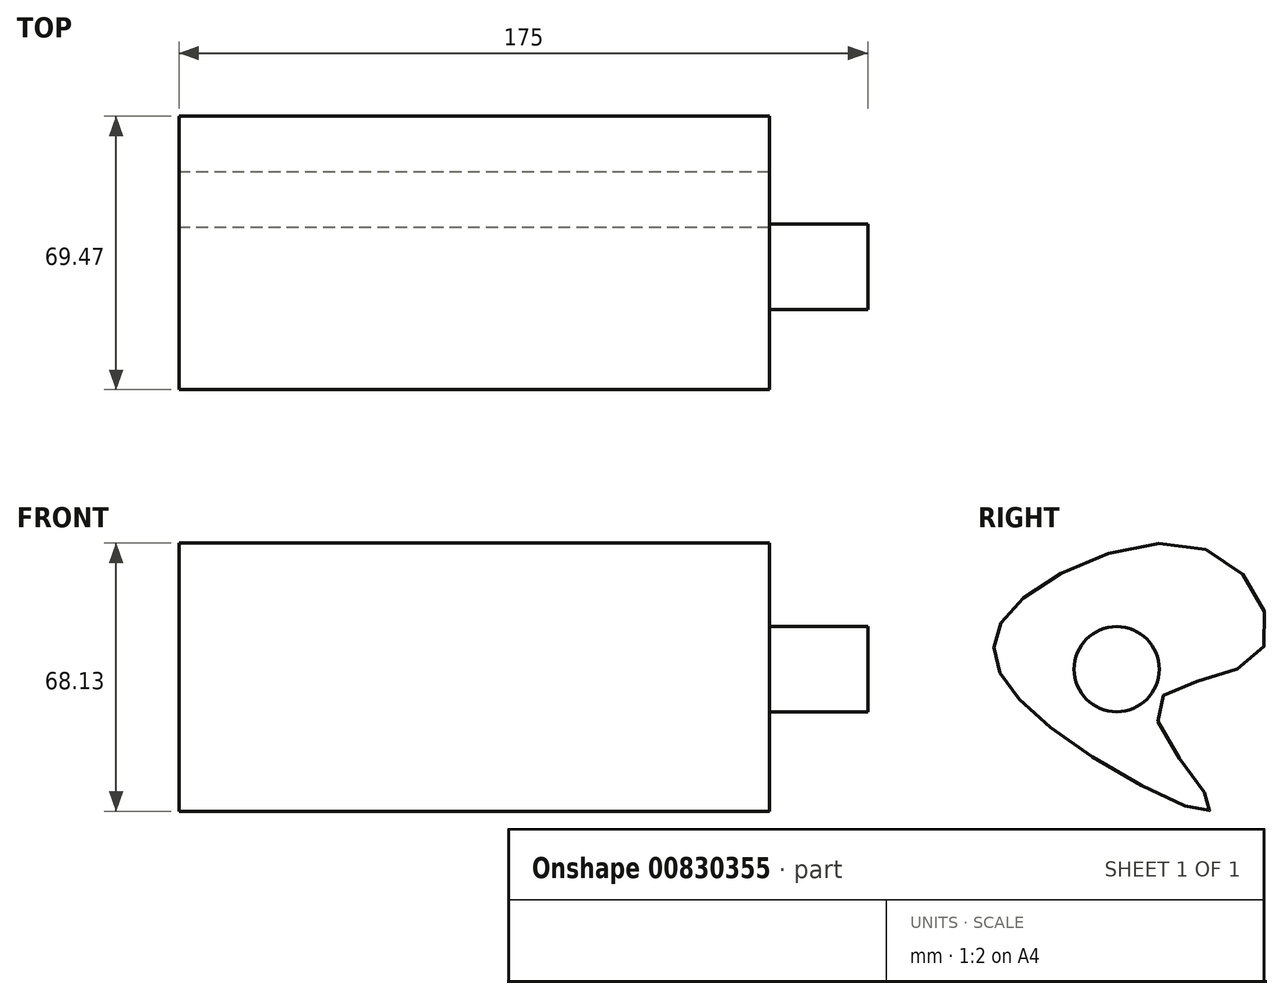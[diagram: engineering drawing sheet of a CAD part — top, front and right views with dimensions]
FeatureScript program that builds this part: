
annotation { "Feature Type Name" : "Feature", "Feature Type Description" : "" }
export const myFeature = defineFeature(function(context is Context, id is Id, definition is map)
    precondition{}
    {
        {
            var Q0;
            Q0=qCreatedBy(makeId("Right.planeOp"),FACE);
            var sketch = newSketch(context, id + "F0", { "sketchPlane" : qUnion([Q0])});
            skFitSpline(sketch, "E0", {"points": [v(-23.68, 8.44) * mm, v(-30.94, -6.8) * mm, v(-8.8, -30.21) * mm, v(24.04, -44.73) * mm, v(10.07, -18.96) * mm, v(36.02, -6.08) * mm, v(24.22, 20.23) * mm, v(-23.68, 8.44) * mm]});
            skSolve(sketch);
        }
        {
            var Q0;
            Q0=makeQuery(id+"F0.imprint","IMPRINT",FACE,{"disambiguationData":[TD([[makeQuery(id+"F0.imprint","IMPRINT",EDGE,{"derivedFrom":sQuery(id+"F0.wireOp",EDGE,"E0")}),1.0]])]});
            extrude(context, id + "F1", {"entities" : qUnion([Q0]), "depth" : 150 * mm, "offsetDistance" : 25 * mm});
        }
        {
            var Q0;
            Q0=makeQuery(id+"F1.opExtrude","CAP_FACE",FACE,{"disambiguationData":[OSD([sQuery(id+"F0.wireOp",EDGE,"E0")])],"isStart":false});
            var sketch = newSketch(context, id + "F2", { "sketchPlane" : qUnion([Q0])});
            skCircle(sketch, "E1", {"center": v(0, -9.62) * mm, "radius": 10.82 * mm});
            skSolve(sketch);
        }
        {
            var Q0;
            Q0=makeQuery(id+"F2.imprint","IMPRINT",FACE,{"disambiguationData":[TD([[makeQuery(id+"F2.imprint","IMPRINT",EDGE,{"derivedFrom":sQuery(id+"F2.wireOp",EDGE,"E1")}),1.0]])]});
            extrude(context, id + "F3", {"entities" : qUnion([Q0]), "operationType" : NewBodyOperationType.ADD, "depth" : 25 * mm, "offsetDistance" : 25 * mm});
        }
    });
